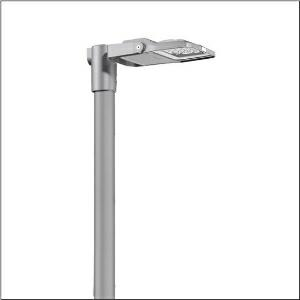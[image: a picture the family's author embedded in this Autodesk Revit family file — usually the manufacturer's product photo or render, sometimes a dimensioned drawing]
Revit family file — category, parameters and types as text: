
# Revit family: floodlight_fl_21_iq_micro___pl64_5xa7761a2e3a_b98d
name_source: partatom
category: Lighting Fixtures
units: mm (PartAtom-declared; Revit-internal decimal feet)

## family parameters
Cut with Voids When Loaded = No
Host = Face
Light Source = No
Part Type = Normal
Room Calculation Point = No
Round Connector Dimension = Use Diameter
Shared = No

## types (1)
- --- (1 x LED, 2870 lm, 23.1 W, 3000K)
    Apparent Load = 23 VA
    CIE Flux Codes = 28 80 98 100 100
    Color Rendering = 70
    Color Temperature = 3000K
    Default Elevation = 1800 mm
    Description = Floodlight FL 21 iQ micro, floodlight, primary light control with lens, of PMMA, primary optical cover: protective disc, of toughened safety glass, transparent, light distribution: PL64, light emission: direct distribution, installation type: surface-mounted, lamps: LED, High Power LED, rated values: 2.870lm | 23,1W | 124,2lm/W (begin service life); end service life: 2.870lm | 23,8W; at 50% lumin. flux: 1.435lm | 11W | 130,5lm/W, colour temperature: 3000K, colour rendering: CRI > 70, light colour: 730, light setting 1 begin service life: 100% | 2.870lm | 23,1W | 124,2lm/W | 3.000K, light setting 1 end service life: 23,8W, further light settings possible, control: optimised constant luminous flux control (CLO 2.0), Desk-Remote (wireless, voltage-free reading and setting of iQ features in the workshop via application-optimized NFC function/RFID function), Light-Fading, Smart-Wire, Night-Set, Lumen-Switch, Temp-Guard, Auto-Match, pre-setting: linear dimming characteristic, with terminal, 6-pole, mains connection: 220..240V, AC, 50/60Hz, luminaire housing, of diecast aluminium, powder-coated, SITECO metallic grey (DB 702S), corrosivity category C5 mid according to DIN EN ISO 12944suitable for swimming poolschlorine-resistant, sealing non-destructively replaceable, please order mast flange separately, mast bracket, of steel, galvanised, powder-coated, SITECO metallic grey (DB 702S), protection rating (complete): IP66, insulation class (complete): insulation class II (safety insulation), certification: CE, ENEC, VDE, protection symbol: D, impact resistance: IK07, permissible operating ambient temperature: -40..+40°C, permissible operating ambient temperature for outdoor applications: -40..+50°C, standard: DIN EN 12944, LABS conformity tested according to VDMA 24364:2018-05, packaging unit: 1 piece

Light Distribution: PL64
    Height = 65 mm
    Lamp = 1 x LED
    Lamp Light Flux = 2870 lm
    Lamp Power = 23.1 W
    Lamp count = 1
    Length = 312 mm
    Luminous efficacy = 124 lm/W
    Manufacturer = Siteco
    ModVariant = No
    Model = 5XA7761A2E3A
    Number of Poles = 1
    OnlyDefault = Yes
    Power Factor = 1
    Product Name = Floodlight FL 21 iQ micro | PL64
    Product group = floodlight | pylon top
    ProductGroupID = 6101
    Protection Class = Protection class II
    Protection Degree = IP 66
    RLX_Detail_Level = 1
    RLX_Emergency_Light_Flux = 0 lm
    RLX_Emergency_Type = 0
    RLX_Emergency_Type_DB = No
    RlxData = <blob elided: 102041 chars, md5=72e9a9d7>
    Socket = socket
    Standby Power = 0 W
    System Light Flux = 2870 lm
    System Power = 23 W
    Type Comments = factory setting: luminous flux: 100 % | dim-lin: 254 | 455 mA
    Type Image = l_1007121.jpg
    URL = http://relux.com
    VarID = @adj_179597
    Voltage = 0 V
    Weight = 0.00 kg
    Width = 230 mm

## geometry (parser evidence)
native form markers: Blend x4, Sweep x12
no freeform markers — native parametric forms only
